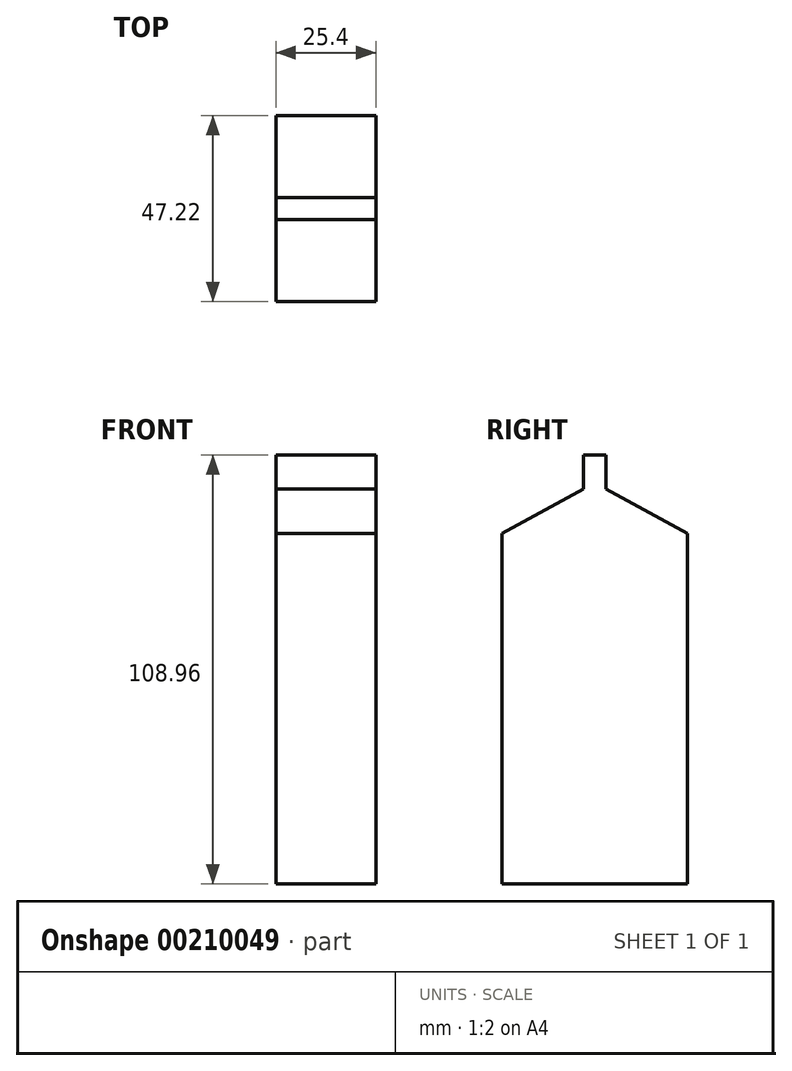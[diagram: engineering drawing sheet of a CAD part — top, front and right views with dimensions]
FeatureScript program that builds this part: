
annotation { "Feature Type Name" : "Feature", "Feature Type Description" : "" }
export const myFeature = defineFeature(function(context is Context, id is Id, definition is map)
    precondition{}
    {
        {
            var Q0;
            Q0=qCreatedBy(makeId("Right.planeOp"),FACE);
            var sketch = newSketch(context, id + "F0", { "sketchPlane" : qUnion([Q0])});
            skLineSegment(sketch, "E0.top", {"start": v(-23.6, -44.5) * mm, "end": v(23.6, -44.5) * mm});
            skLineSegment(sketch, "E0.left", {"start": v(-23.6, 44.5) * mm, "end": v(-23.6, -44.5) * mm});
            skLineSegment(sketch, "E0.right", {"start": v(23.6, 44.5) * mm, "end": v(23.6, -44.5) * mm});
            skPoint(sketch, "E0.middle", {"position": v(0, 0) * mm});
            skLineSegment(sketch, "E1", {"start": v(23.6, 44.5) * mm, "end": v(2.83, 55.8) * mm});
            skLineSegment(sketch, "E2", {"start": v(2.83, 55.8) * mm, "end": v(2.83, 64.47) * mm});
            skLineSegment(sketch, "E3", {"start": v(2.83, 64.47) * mm, "end": v(0, 64.47) * mm});
            skLineSegment(sketch, "E4.MirrorCS", {"start": v(-23.6, 44.5) * mm, "end": v(-2.83, 55.8) * mm});
            skLineSegment(sketch, "E5.MirrorCS", {"start": v(-2.83, 55.8) * mm, "end": v(-2.83, 64.47) * mm});
            skLineSegment(sketch, "E6.MirrorCS", {"start": v(-2.83, 64.47) * mm, "end": v(0, 64.47) * mm});
            skSolve(sketch);
        }
        {
            var Q0;
            Q0=makeQuery(id+"F0.imprint","IMPRINT",FACE,{"disambiguationData":[TD([[makeQuery(id+"F0.imprint","IMPRINT",EDGE,{"derivedFrom":sQuery(id+"F0.wireOp",EDGE,"E0.top")}),1.0]])]});
            extrude(context, id + "F1", {"entities" : qUnion([Q0]), "depth" : 25.4 * mm});
        }
    });
